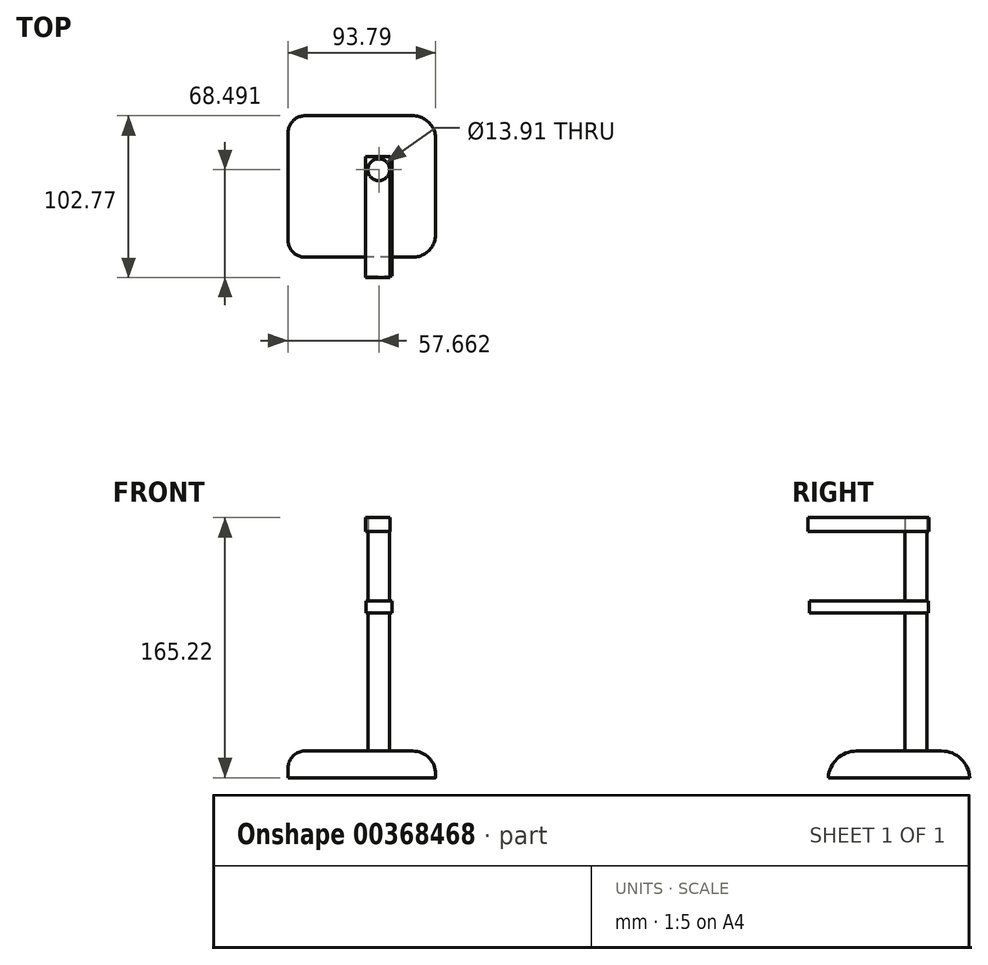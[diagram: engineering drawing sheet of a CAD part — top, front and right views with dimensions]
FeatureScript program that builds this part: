
annotation { "Feature Type Name" : "Feature", "Feature Type Description" : "" }
export const myFeature = defineFeature(function(context is Context, id is Id, definition is map)
    precondition{}
    {
        {
            var Q0;
            Q0=qCreatedBy(makeId("Top.planeOp"),FACE);
            var sketch = newSketch(context, id + "F0", { "sketchPlane" : qUnion([Q0])});
            skLineSegment(sketch, "E0.bottom", {"start": v(55.68, -39.48) * mm, "end": v(-38.1, -39.48) * mm});
            skLineSegment(sketch, "E0.top", {"start": v(55.68, 50.36) * mm, "end": v(-38.1, 50.36) * mm});
            skLineSegment(sketch, "E0.left", {"start": v(55.68, -39.48) * mm, "end": v(55.68, 50.36) * mm});
            skLineSegment(sketch, "E0.right", {"start": v(-38.1, -39.48) * mm, "end": v(-38.1, 50.36) * mm});
            skSolve(sketch);
        }
        {
            var Q0;
            Q0=makeQuery(id+"F0.imprint","IMPRINT",FACE,{"disambiguationData":[TD([[makeQuery(id+"F0.imprint","IMPRINT",EDGE,{"derivedFrom":sQuery(id+"F0.wireOp",EDGE,"E0.bottom")}),-1.0]])]});
            extrude(context, id + "F1", {"entities" : qUnion([Q0]), "depth" : 16.95 * mm});
        }
        {
            var Q0;
            Q0=makeQuery(id+"F1.opExtrude","CAP_EDGE",EDGE,{"disambiguationData":[OSD([sQuery(id+"F0.wireOp",EDGE,"E0.bottom")])],"isStart":false});
            var Q1;
            Q1=makeQuery(id+"F1.opExtrude","CAP_EDGE",EDGE,{"disambiguationData":[OSD([sQuery(id+"F0.wireOp",EDGE,"E0.top")])],"isStart":false});
            fillet(context, id + "F2", {"entities" : qUnion([Q0, Q1]), "radius" : 17.94 * mm, "tangentPropagation" : true, "allowEdgeOverflow" : false});
        }
        {
            var Q0;
            Q0=makeQuery(id+"F1.opExtrude","CAP_EDGE",EDGE,{"disambiguationData":[OSD([sQuery(id+"F0.wireOp",EDGE,"E0.right")])],"isStart":false});
            var Q1;
            Q1=makeQuery(id+"F2.opFillet","BLEND_EDGE",EDGE,{"blendedFrom":[makeQuery(id+"F1.opExtrude","CAP_EDGE",EDGE,{"disambiguationData":[OSD([sQuery(id+"F0.wireOp",EDGE,"E0.bottom")])],"isStart":false}),makeQuery(id+"F1.opExtrude","SWEPT_FACE",FACE,{"disambiguationData":[OSD([sQuery(id+"F0.wireOp",EDGE,"E0.right")])]})],"blendedInto":[makeQuery(id+"F1.opExtrude","SWEPT_FACE",FACE,{"disambiguationData":[OSD([sQuery(id+"F0.wireOp",EDGE,"E0.right")])]})]});
            var Q2;
            Q2=makeQuery(id+"F2.opFillet","BLEND_EDGE",EDGE,{"blendedFrom":[makeQuery(id+"F1.opExtrude","CAP_EDGE",EDGE,{"disambiguationData":[OSD([sQuery(id+"F0.wireOp",EDGE,"E0.top")])],"isStart":false}),makeQuery(id+"F1.opExtrude","SWEPT_FACE",FACE,{"disambiguationData":[OSD([sQuery(id+"F0.wireOp",EDGE,"E0.right")])]})],"blendedInto":[makeQuery(id+"F1.opExtrude","SWEPT_FACE",FACE,{"disambiguationData":[OSD([sQuery(id+"F0.wireOp",EDGE,"E0.right")])]})]});
            fillet(context, id + "F3", {"entities" : qUnion([Q0, Q1, Q2]), "radius" : 10.8 * mm, "tangentPropagation" : true, "allowEdgeOverflow" : false});
        }
        {
            var Q0;
            Q0=makeQuery(id+"F2.opFillet","BLEND_EDGE",EDGE,{"blendedFrom":[makeQuery(id+"F1.opExtrude","CAP_EDGE",EDGE,{"disambiguationData":[OSD([sQuery(id+"F0.wireOp",EDGE,"E0.top")])],"isStart":false}),makeQuery(id+"F1.opExtrude","SWEPT_FACE",FACE,{"disambiguationData":[OSD([sQuery(id+"F0.wireOp",EDGE,"E0.left")])]})],"blendedInto":[makeQuery(id+"F1.opExtrude","SWEPT_FACE",FACE,{"disambiguationData":[OSD([sQuery(id+"F0.wireOp",EDGE,"E0.left")])]})]});
            var Q1;
            Q1=makeQuery(id+"F1.opExtrude","CAP_EDGE",EDGE,{"disambiguationData":[OSD([sQuery(id+"F0.wireOp",EDGE,"E0.left")])],"isStart":false});
            var Q2;
            Q2=makeQuery(id+"F2.opFillet","BLEND_EDGE",EDGE,{"blendedFrom":[makeQuery(id+"F1.opExtrude","CAP_EDGE",EDGE,{"disambiguationData":[OSD([sQuery(id+"F0.wireOp",EDGE,"E0.bottom")])],"isStart":false}),makeQuery(id+"F1.opExtrude","SWEPT_FACE",FACE,{"disambiguationData":[OSD([sQuery(id+"F0.wireOp",EDGE,"E0.left")])]})],"blendedInto":[makeQuery(id+"F1.opExtrude","SWEPT_FACE",FACE,{"disambiguationData":[OSD([sQuery(id+"F0.wireOp",EDGE,"E0.left")])]})]});
            fillet(context, id + "F4", {"entities" : qUnion([Q0, Q1, Q2]), "radius" : 14.62 * mm, "tangentPropagation" : true, "allowEdgeOverflow" : false});
        }
        {
            var Q0;
            Q0=qCreatedBy(makeId("Top.planeOp"),FACE);
            var sketch = newSketch(context, id + "F5", { "sketchPlane" : qUnion([Q0])});
            skCircle(sketch, "E1", {"center": v(19.55, 16.08) * mm, "radius": 6.96 * mm});
            skSolve(sketch);
        }
        {
            var Q0;
            Q0 = qSketchRegion(id + "F5", true);
            extrude(context, id + "F6", {"entities" : qUnion([Q0]), "operationType" : NewBodyOperationType.ADD, "depth" : 112.93 * mm});
        }
        {
            var Q0;
            Q0=makeQuery(id+"F6.opExtrude","CAP_FACE",FACE,{"disambiguationData":[OSD([sQuery(id+"F5.wireOp",EDGE,"E1")])],"isStart":false});
            cPlane(context, id + "F7", {"entities" : qUnion([Q0]), "cplaneType" : CPlaneType.OFFSET, "offset" : 0.54 * mm, "oppositeDirection" : true, "width" : 152.4 * mm, "height" : 152.4 * mm});
        }
        {
            var Q0;
            Q0=qCreatedBy(id+"F7.planeOp",FACE);
            var sketch = newSketch(context, id + "F8", { "sketchPlane" : qUnion([Q0])});
            skLineSegment(sketch, "E2.bottom", {"start": v(11.6, 24.24) * mm, "end": v(28.05, 24.24) * mm});
            skLineSegment(sketch, "E2.top", {"start": v(11.6, -51.41) * mm, "end": v(28.05, -51.41) * mm});
            skLineSegment(sketch, "E2.left", {"start": v(11.6, 24.24) * mm, "end": v(11.6, -51.41) * mm});
            skLineSegment(sketch, "E2.right", {"start": v(28.05, 24.24) * mm, "end": v(28.05, -51.41) * mm});
            skSolve(sketch);
        }
        {
            var Q0;
            Q0=makeQuery(id+"F8.imprint","IMPRINT",FACE,{"disambiguationData":[TD([[makeQuery(id+"F8.imprint","IMPRINT",EDGE,{"derivedFrom":sQuery(id+"F8.wireOp",EDGE,"E2.bottom")}),-1.0]])]});
            extrude(context, id + "F9", {"entities" : qUnion([Q0]), "operationType" : NewBodyOperationType.ADD, "oppositeDirection" : true, "depth" : 7.7 * mm});
        }
        {
            var Q0;
            Q0=makeQuery(id+"F6.opExtrude","CAP_FACE",FACE,{"disambiguationData":[OSD([sQuery(id+"F5.wireOp",EDGE,"E1")])],"isStart":false});
            extrude(context, id + "F10", {"entities" : qUnion([Q0]), "operationType" : NewBodyOperationType.ADD, "depth" : 43.54 * mm});
        }
        {
            var Q0;
            Q0=makeQuery(id+"F10.opExtrude","CAP_FACE",FACE,{"disambiguationData":[OSD([sQuery(id+"F5.wireOp",EDGE,"E1")])],"isStart":false});
            var sketch = newSketch(context, id + "F11", { "sketchPlane" : qUnion([Q0])});
            skLineSegment(sketch, "E3.bottom", {"start": v(11.19, 24.45) * mm, "end": v(26.75, 24.45) * mm});
            skLineSegment(sketch, "E3.top", {"start": v(11.19, -52.41) * mm, "end": v(26.75, -52.41) * mm});
            skLineSegment(sketch, "E3.left", {"start": v(11.19, 24.45) * mm, "end": v(11.19, -52.41) * mm});
            skLineSegment(sketch, "E3.right", {"start": v(26.75, 24.45) * mm, "end": v(26.75, -52.41) * mm});
            skSolve(sketch);
        }
        {
            var Q0;
            Q0=makeQuery(id+"F11.imprint","IMPRINT",FACE,{"disambiguationData":[TD([[makeQuery(id+"F11.imprint","IMPRINT",EDGE,{"derivedFrom":sQuery(id+"F11.wireOp",EDGE,"E3.bottom")}),-1.0]])]});
            extrude(context, id + "F12", {"entities" : qUnion([Q0]), "depth" : 8.75 * mm});
        }
    });
